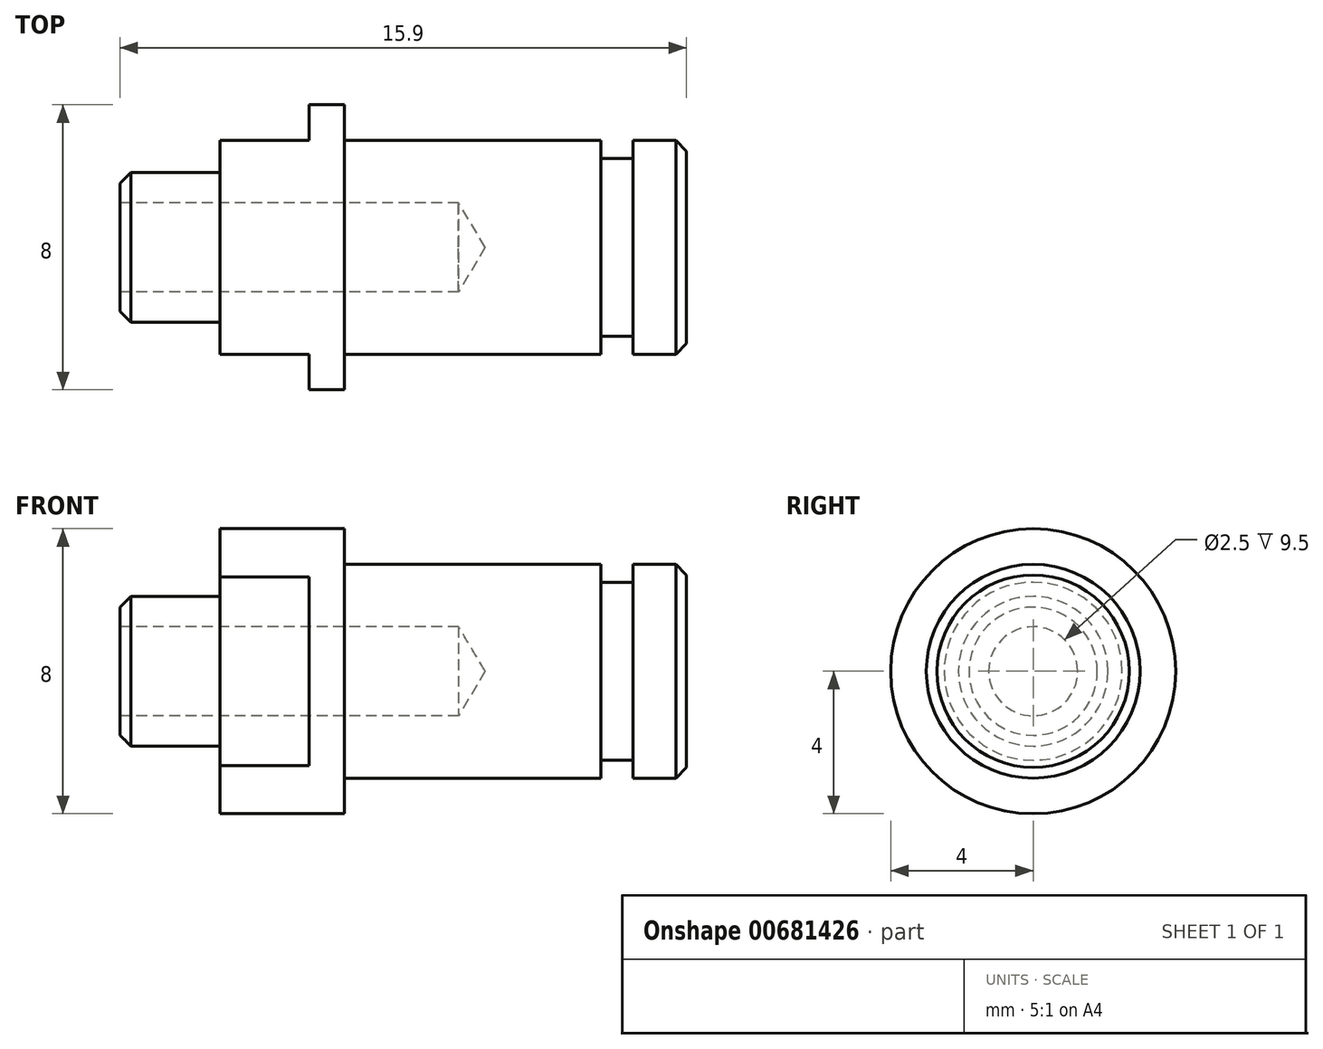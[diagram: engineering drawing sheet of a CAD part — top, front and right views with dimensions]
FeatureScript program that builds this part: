
annotation { "Feature Type Name" : "Feature", "Feature Type Description" : "" }
export const myFeature = defineFeature(function(context is Context, id is Id, definition is map)
    precondition{}
    {
        {
            var Q0;
            Q0=qCreatedBy(makeId("Front.planeOp"),FACE);
            var sketch = newSketch(context, id + "F0", { "sketchPlane" : qUnion([Q0])});
            skLineSegment(sketch, "E0", {"start": v(-5.93, 0) * mm, "end": v(-5.93, 2.1) * mm});
            skLineSegment(sketch, "E1", {"start": v(-5.93, 2.1) * mm, "end": v(-3.13, 2.1) * mm});
            skLineSegment(sketch, "E2", {"start": v(-3.13, 2.1) * mm, "end": v(-3.13, 4) * mm});
            skLineSegment(sketch, "E3", {"start": v(-3.13, 4) * mm, "end": v(0.37, 4) * mm});
            skLineSegment(sketch, "E4", {"start": v(0.37, 4) * mm, "end": v(0.37, 3) * mm});
            skLineSegment(sketch, "E5", {"start": v(0.37, 3) * mm, "end": v(9.97, 3) * mm});
            skLineSegment(sketch, "E6", {"start": v(9.97, 3) * mm, "end": v(9.97, 0) * mm});
            skLineSegment(sketch, "E7", {"start": v(9.97, 0) * mm, "end": v(-5.93, 0) * mm});
            skSolve(sketch);
        }
        {
            var Q0;
            Q0 = qSketchRegion(id + "F0", true);
            var Q1;
            Q1=sQuery(id+"F0.wireOp",EDGE,"E7");
            revolve(context, id + "F1", {"entities" : qUnion([Q0]), "axis" : qUnion([Q1]), "revolveType" : RevolveType.FULL});
        }
        {
            var Q0;
            Q0=makeQuery(id+"F1.opRevolve","SWEPT_FACE",FACE,{"disambiguationData":[OSD([sQuery(id+"F0.wireOp",EDGE,"E2")])]});
            var sketch = newSketch(context, id + "F2", { "sketchPlane" : qUnion([Q0])});
            skLineSegment(sketch, "E8.bottom", {"start": v(3, 5) * mm, "end": v(7, 5) * mm});
            skLineSegment(sketch, "E8.top", {"start": v(3, -5) * mm, "end": v(7, -5) * mm});
            skLineSegment(sketch, "E8.left", {"start": v(3, 5) * mm, "end": v(3, -5) * mm});
            skLineSegment(sketch, "E8.right", {"start": v(7, 5) * mm, "end": v(7, -5) * mm});
            skLineSegment(sketch, "E9.bottom", {"start": v(-3, 5) * mm, "end": v(-7, 5) * mm});
            skLineSegment(sketch, "E9.top", {"start": v(-3, -5) * mm, "end": v(-7, -5) * mm});
            skLineSegment(sketch, "E9.left", {"start": v(-3, 5) * mm, "end": v(-3, -5) * mm});
            skLineSegment(sketch, "E9.right", {"start": v(-7, 5) * mm, "end": v(-7, -5) * mm});
            skSolve(sketch);
        }
        {
            var Q0;
            Q0 = qSketchRegion(id + "F2", true);
            extrude(context, id + "F3", {"entities" : qUnion([Q0]), "operationType" : NewBodyOperationType.REMOVE, "oppositeDirection" : true, "depth" : 2.5 * mm, "offsetDistance" : 25 * mm});
        }
        {
            var Q0;
            Q0=makeQuery(id+"F1.opRevolve","SWEPT_FACE",FACE,{"disambiguationData":[OSD([sQuery(id+"F0.wireOp",EDGE,"E0")])]});
            var sketch = newSketch(context, id + "F4", { "sketchPlane" : qUnion([Q0])});
            skPoint(sketch, "E10", {"position": v(0, 0) * mm});
            skSolve(sketch);
        }
        {
            var Q0;
            Q0=sQuery(id+"F4.wireOp",VERTEX,"E10");
            var Q1;
            Q1=makeQuery(id+"F1.opRevolve","SWEPT_BODY",BODY,{"disambiguationData":[OSD([sQuery(id+"F0.wireOp",EDGE,"E0"),sQuery(id+"F0.wireOp",EDGE,"E1"),sQuery(id+"F0.wireOp",EDGE,"E2"),sQuery(id+"F0.wireOp",EDGE,"E3"),sQuery(id+"F0.wireOp",EDGE,"E4"),sQuery(id+"F0.wireOp",EDGE,"E5"),sQuery(id+"F0.wireOp",EDGE,"E6"),sQuery(id+"F0.wireOp",EDGE,"E7")])]});
            hole(context, id + "F5", {"style" : HoleStyle.SIMPLE, "endStyle" : HoleEndStyle.BLIND, "standardTappedOrClearance" : lookupTablePath({ "standard" : "ISO", "engagement" : "75%", "pitch" : "0.5 mm", "size" : "M3", "type" : "Tapped" }), "standardBlindInLast" : lookupTablePath({ "standard" : "ISO", "engagement" : "75%", "pitch" : "0.5 mm", "size" : "M3", "type" : "Tapped" }), "holeDiameter" : 2.5 * mm, "majorDiameter" : 3 * mm, "showTappedDepth" : true, "holeDepth" : 9.5 * mm, "tappedDepth" : 8 * mm, "tapClearance" : 3, "startFromSketch" : true, "locations" : qUnion([Q0]), "scope" : qUnion([Q1])});
        }
        {
            var Q0;
            Q0=qCreatedBy(makeId("Front.planeOp"),FACE);
            var sketch = newSketch(context, id + "F6", { "sketchPlane" : qUnion([Q0])});
            skLineSegment(sketch, "E11.bottom", {"start": v(7.57, 4.5) * mm, "end": v(8.47, 4.5) * mm});
            skLineSegment(sketch, "E11.top", {"start": v(7.57, 2.5) * mm, "end": v(8.47, 2.5) * mm});
            skLineSegment(sketch, "E11.left", {"start": v(7.57, 4.5) * mm, "end": v(7.57, 2.5) * mm});
            skLineSegment(sketch, "E11.right", {"start": v(8.47, 4.5) * mm, "end": v(8.47, 2.5) * mm});
            skSolve(sketch);
        }
        {
            var Q0;
            Q0 = qSketchRegion(id + "F6", true);
            var Q1;
            Q1=sQuery(id+"F0.wireOp",EDGE,"E7");
            revolve(context, id + "F7", {"operationType" : NewBodyOperationType.REMOVE, "entities" : qUnion([Q0]), "axis" : qUnion([Q1]), "revolveType" : RevolveType.FULL, "oppositeDirection" : true});
        }
        {
            var Q0;
            Q0=makeQuery(id+"F1.opRevolve","SWEPT_EDGE",EDGE,{"disambiguationData":[OSD([sQuery(id+"F0.wireOp",EDGE,"E5"),sQuery(id+"F0.wireOp",EDGE,"E6")])]});
            var Q1;
            Q1=makeQuery(id+"F1.opRevolve","SWEPT_EDGE",EDGE,{"disambiguationData":[OSD([sQuery(id+"F0.wireOp",EDGE,"E0"),sQuery(id+"F0.wireOp",EDGE,"E1")])]});
            chamfer(context, id + "F8", {"entities" : qUnion([Q0, Q1]), "width" : 0.3 * mm, "tangentPropagation" : true});
        }
    });
